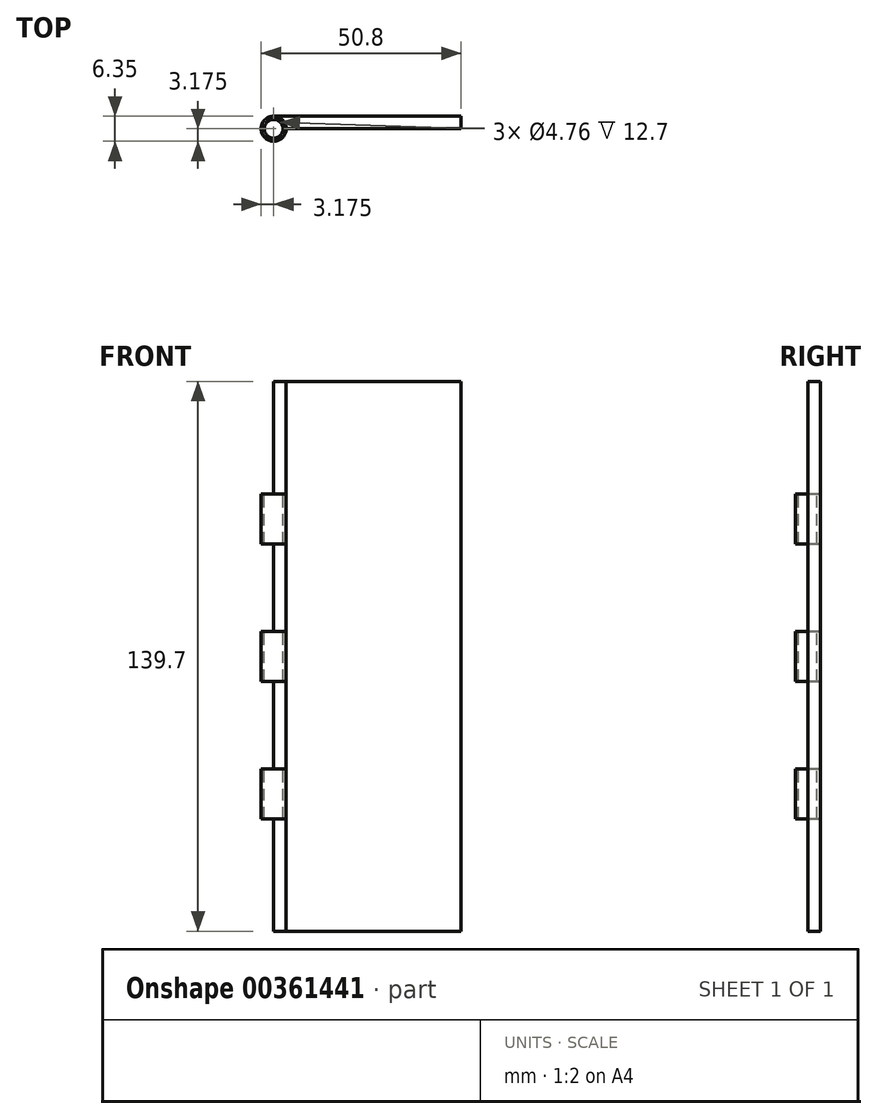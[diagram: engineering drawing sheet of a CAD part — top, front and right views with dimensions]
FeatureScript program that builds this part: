
annotation { "Feature Type Name" : "Feature", "Feature Type Description" : "" }
export const myFeature = defineFeature(function(context is Context, id is Id, definition is map)
    precondition{}
    {
        {
            var Q0;
            Q0=qCreatedBy(makeId("Top.planeOp"),FACE);
            var sketch = newSketch(context, id + "F0", { "sketchPlane" : qUnion([Q0])});
            skLineSegment(sketch, "E0", {"start": v(0, 0) * mm, "end": v(-47.62, 0) * mm});
            skArc(sketch, "E1", {"start": v(-47.62, 0) * mm, "mid": v(-49.87, -5.42) * mm, "end": v(-44.45, -3.18) * mm});
            skLineSegment(sketch, "E2", {"start": v(-44.45, -3.18) * mm, "end": v(0, -3.18) * mm});
            skLineSegment(sketch, "E3", {"start": v(0, -3.18) * mm, "end": v(0, 0) * mm});
            skLineSegment(sketch, "E4", {"start": v(-44.45, -5.44) * mm, "end": v(-44.45, -2.69) * mm, "construction": true});
            skSolve(sketch);
        }
        {
            var Q0;
            Q0=makeQuery(id+"F0.imprint","IMPRINT",FACE,{"disambiguationData":[TD([[makeQuery(id+"F0.imprint","IMPRINT",EDGE,{"derivedFrom":sQuery(id+"F0.wireOp",EDGE,"E0")}),1.0]])]});
            extrude(context, id + "F1", {"entities" : qUnion([Q0]), "depth" : 139.7 * mm});
        }
        {
            var Q0;
            Q0=makeQuery(id+"F1.opExtrude","CAP_FACE",FACE,{"disambiguationData":[OSD([sQuery(id+"F0.wireOp",EDGE,"E0"),sQuery(id+"F0.wireOp",EDGE,"E1"),sQuery(id+"F0.wireOp",EDGE,"E2"),sQuery(id+"F0.wireOp",EDGE,"E3")])],"isStart":false});
            var sketch = newSketch(context, id + "F2", { "sketchPlane" : qUnion([Q0])});
            skCircle(sketch, "E5", {"center": v(-47.62, -3.18) * mm, "radius": 3.18 * mm});
            skSolve(sketch);
        }
        {
            var Q0;
            {var subQ0=sQuery(id+"F2.wireOp",EDGE,"E5");var subQ1=makeQuery(id+"F2.imprint","INTERSECT",VERTEX,{"derivedFrom":[makeQuery(id+"F1.opExtrude","CAP_EDGE",EDGE,{"disambiguationData":[OSD([sQuery(id+"F0.wireOp",EDGE,"E0")])],"isStart":false}),subQ0]});Q0=makeQuery(id+"F2.imprint","IMPRINT",FACE,{"disambiguationData":[TD([[makeQuery(id+"F2.imprint","IMPRINT",EDGE,{"disambiguationData":[TD([[subQ1,1.0]])],"derivedFrom":subQ0}),1.0]])]});}
            extrude(context, id + "F3", {"entities" : qUnion([Q0]), "operationType" : NewBodyOperationType.REMOVE, "endBound" : BoundingType.THROUGH_ALL, "oppositeDirection" : true, "depth" : 25.4 * mm});
        }
        {
            var Q0;
            Q0=makeQuery(id+"F1.opExtrude","CAP_FACE",FACE,{"disambiguationData":[OSD([sQuery(id+"F0.wireOp",EDGE,"E0"),sQuery(id+"F0.wireOp",EDGE,"E1"),sQuery(id+"F0.wireOp",EDGE,"E2"),sQuery(id+"F0.wireOp",EDGE,"E3")])],"isStart":false});
            var Q1;
            Q1=makeQuery(id+"F1.opExtrude","CAP_FACE",FACE,{"disambiguationData":[OSD([sQuery(id+"F0.wireOp",EDGE,"E0"),sQuery(id+"F0.wireOp",EDGE,"E1"),sQuery(id+"F0.wireOp",EDGE,"E2"),sQuery(id+"F0.wireOp",EDGE,"E3")])],"isStart":true});
            cPlane(context, id + "F4", {"entities" : qUnion([Q0, Q1]), "cplaneType" : CPlaneType.MID_PLANE, "offset" : 25.4 * mm, "width" : 152.4 * mm, "height" : 152.4 * mm});
        }
        {
            var Q0;
            Q0=qCreatedBy(id+"F4.planeOp",FACE);
            var Q1;
            Q1=makeQuery(id+"F1.opExtrude","CAP_FACE",FACE,{"disambiguationData":[OSD([sQuery(id+"F0.wireOp",EDGE,"E0"),sQuery(id+"F0.wireOp",EDGE,"E1"),sQuery(id+"F0.wireOp",EDGE,"E2"),sQuery(id+"F0.wireOp",EDGE,"E3")])],"isStart":false});
            cPlane(context, id + "F5", {"entities" : qUnion([Q0, Q1]), "cplaneType" : CPlaneType.MID_PLANE, "offset" : 25.4 * mm, "width" : 152.4 * mm, "height" : 152.4 * mm});
        }
        {
            var Q0;
            Q0=qCreatedBy(id+"F4.planeOp",FACE);
            var Q1;
            Q1=makeQuery(id+"F1.opExtrude","CAP_FACE",FACE,{"disambiguationData":[OSD([sQuery(id+"F0.wireOp",EDGE,"E0"),sQuery(id+"F0.wireOp",EDGE,"E1"),sQuery(id+"F0.wireOp",EDGE,"E2"),sQuery(id+"F0.wireOp",EDGE,"E3")])],"isStart":true});
            cPlane(context, id + "F6", {"entities" : qUnion([Q0, Q1]), "cplaneType" : CPlaneType.MID_PLANE, "offset" : 25.4 * mm, "width" : 152.4 * mm, "height" : 152.4 * mm});
        }
        {
            var Q0;
            Q0=qCreatedBy(id+"F5.planeOp",FACE);
            var sketch = newSketch(context, id + "F7", { "sketchPlane" : qUnion([Q0])});
            skCircle(sketch, "E6", {"center": v(-47.62, -3.18) * mm, "radius": 3.18 * mm});
            skSolve(sketch);
        }
        {
            var Q0;
            Q0=makeQuery(id+"F7.imprint","IMPRINT",FACE,{"disambiguationData":[TD([[makeQuery(id+"F7.imprint","IMPRINT",EDGE,{"derivedFrom":sQuery(id+"F7.wireOp",EDGE,"E6")}),1.0]])]});
            extrude(context, id + "F8", {"entities" : qUnion([Q0]), "operationType" : NewBodyOperationType.ADD, "endBound" : BoundingType.SYMMETRIC, "depth" : 12.7 * mm});
        }
        {
            var Q0;
            Q0=qCreatedBy(id+"F4.planeOp",FACE);
            var sketch = newSketch(context, id + "F9", { "sketchPlane" : qUnion([Q0])});
            skCircle(sketch, "E7", {"center": v(-47.62, -3.18) * mm, "radius": 3.18 * mm});
            skSolve(sketch);
        }
        {
            var Q0;
            Q0=makeQuery(id+"F9.imprint","IMPRINT",FACE,{"disambiguationData":[TD([[makeQuery(id+"F9.imprint","IMPRINT",EDGE,{"derivedFrom":sQuery(id+"F9.wireOp",EDGE,"E7")}),1.0]])]});
            extrude(context, id + "F10", {"entities" : qUnion([Q0]), "operationType" : NewBodyOperationType.ADD, "endBound" : BoundingType.SYMMETRIC, "depth" : 12.7 * mm});
        }
        {
            var Q0;
            Q0=qCreatedBy(id+"F6.planeOp",FACE);
            var sketch = newSketch(context, id + "F11", { "sketchPlane" : qUnion([Q0])});
            skCircle(sketch, "E8", {"center": v(-47.62, -3.18) * mm, "radius": 3.18 * mm});
            skSolve(sketch);
        }
        {
            var Q0;
            Q0=makeQuery(id+"F11.imprint","IMPRINT",FACE,{"disambiguationData":[TD([[makeQuery(id+"F11.imprint","IMPRINT",EDGE,{"derivedFrom":sQuery(id+"F11.wireOp",EDGE,"E8")}),1.0]])]});
            extrude(context, id + "F12", {"entities" : qUnion([Q0]), "operationType" : NewBodyOperationType.ADD, "endBound" : BoundingType.SYMMETRIC, "depth" : 12.7 * mm});
        }
        {
            var Q0;
            Q0=makeQuery(id+"F1.opExtrude","CAP_FACE",FACE,{"disambiguationData":[OSD([sQuery(id+"F0.wireOp",EDGE,"E0"),sQuery(id+"F0.wireOp",EDGE,"E1"),sQuery(id+"F0.wireOp",EDGE,"E2"),sQuery(id+"F0.wireOp",EDGE,"E3")])],"isStart":false});
            var sketch = newSketch(context, id + "F13", { "sketchPlane" : qUnion([Q0])});
            skCircle(sketch, "E9", {"center": v(-47.62, -3.18) * mm, "radius": 2.38 * mm});
            skSolve(sketch);
        }
        {
            var Q0;
            Q0=makeQuery(id+"F13.imprint","IMPRINT",FACE,{"disambiguationData":[TD([[makeQuery(id+"F13.imprint","IMPRINT",EDGE,{"derivedFrom":sQuery(id+"F13.wireOp",EDGE,"E9")}),1.0]])]});
            extrude(context, id + "F14", {"entities" : qUnion([Q0]), "operationType" : NewBodyOperationType.REMOVE, "endBound" : BoundingType.THROUGH_ALL, "oppositeDirection" : true, "depth" : 25.4 * mm});
        }
    });
